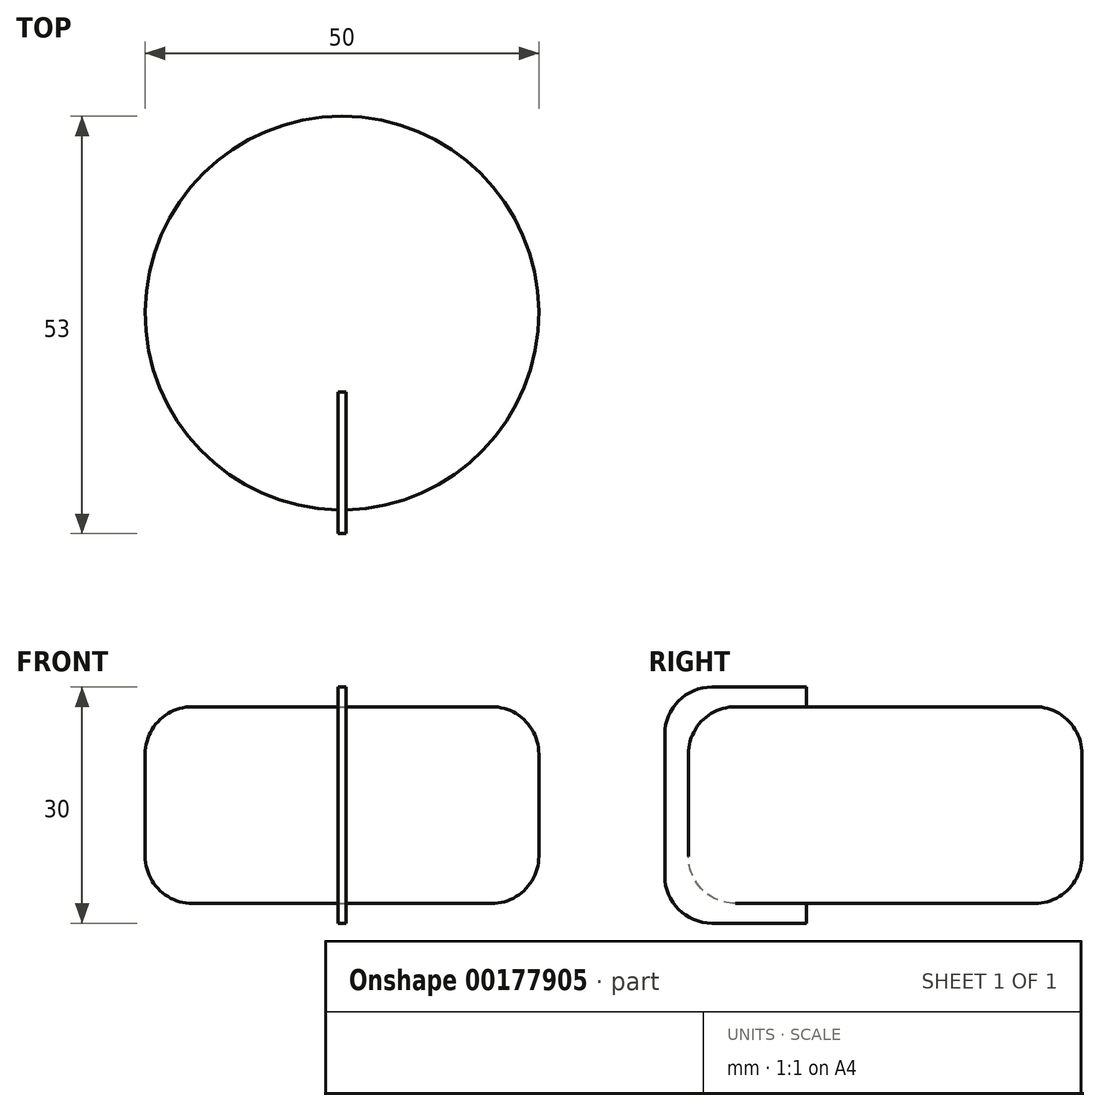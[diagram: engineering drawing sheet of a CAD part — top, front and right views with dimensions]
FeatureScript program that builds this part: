
annotation { "Feature Type Name" : "Feature", "Feature Type Description" : "" }
export const myFeature = defineFeature(function(context is Context, id is Id, definition is map)
    precondition{}
    {
        {
            var Q0;
            Q0=qCreatedBy(makeId("Top.planeOp"),FACE);
            var sketch = newSketch(context, id + "F0", { "sketchPlane" : qUnion([Q0])});
            skCircle(sketch, "E0", {"center": v(0, 0) * mm, "radius": 25 * mm});
            skSolve(sketch);
        }
        {
            var Q0;
            Q0 = qSketchRegion(id + "F0", true);
            extrude(context, id + "F1", {"entities" : qUnion([Q0]), "endBound" : BoundingType.SYMMETRIC, "depth" : 25 * mm});
        }
        {
            var Q0;
            Q0=makeQuery(id+"F1.opExtrude","CAP_EDGE",EDGE,{"disambiguationData":[OSD([sQuery(id+"F0.wireOp",EDGE,"E0")])],"isStart":false});
            var Q1;
            Q1=makeQuery(id+"F1.opExtrude","CAP_EDGE",EDGE,{"disambiguationData":[OSD([sQuery(id+"F0.wireOp",EDGE,"E0")])],"isStart":true});
            fillet(context, id + "F2", {"entities" : qUnion([Q0, Q1]), "radius" : 6 * mm, "tangentPropagation" : true, "allowEdgeOverflow" : false});
        }
        {
            var Q0;
            Q0=qCreatedBy(makeId("Right.planeOp"),FACE);
            var sketch = newSketch(context, id + "F3", { "sketchPlane" : qUnion([Q0])});
            skLineSegment(sketch, "E1", {"start": v(-10, -15) * mm, "end": v(-10, 15) * mm});
            skLineSegment(sketch, "E2", {"start": v(-10, 15) * mm, "end": v(-22, 15) * mm});
            skLineSegment(sketch, "E3", {"start": v(-28, 9) * mm, "end": v(-28, -9) * mm});
            skLineSegment(sketch, "E4", {"start": v(-22, -15) * mm, "end": v(-10, -15) * mm});
            skLineSegment(sketch, "E5", {"start": v(0, 0) * mm, "end": v(-46.95, 0) * mm, "construction": true});
            skPoint(sketch, "E6.visualSharp", {"position": v(-28, 15) * mm});
            skArc(sketch, "E6.filletArc", {"start": v(-22, 15) * mm, "mid": v(-26.24, 13.24) * mm, "end": v(-28, 9) * mm});
            skPoint(sketch, "E7.visualSharp", {"position": v(-28, -15) * mm});
            skArc(sketch, "E7.filletArc", {"start": v(-28, -9) * mm, "mid": v(-26.24, -13.24) * mm, "end": v(-22, -15) * mm});
            skSolve(sketch);
        }
        {
            var Q0;
            Q0 = qSketchRegion(id + "F3", true);
            extrude(context, id + "F4", {"entities" : qUnion([Q0]), "operationType" : NewBodyOperationType.ADD, "endBound" : BoundingType.SYMMETRIC, "depth" : 1 * mm});
        }
    });
